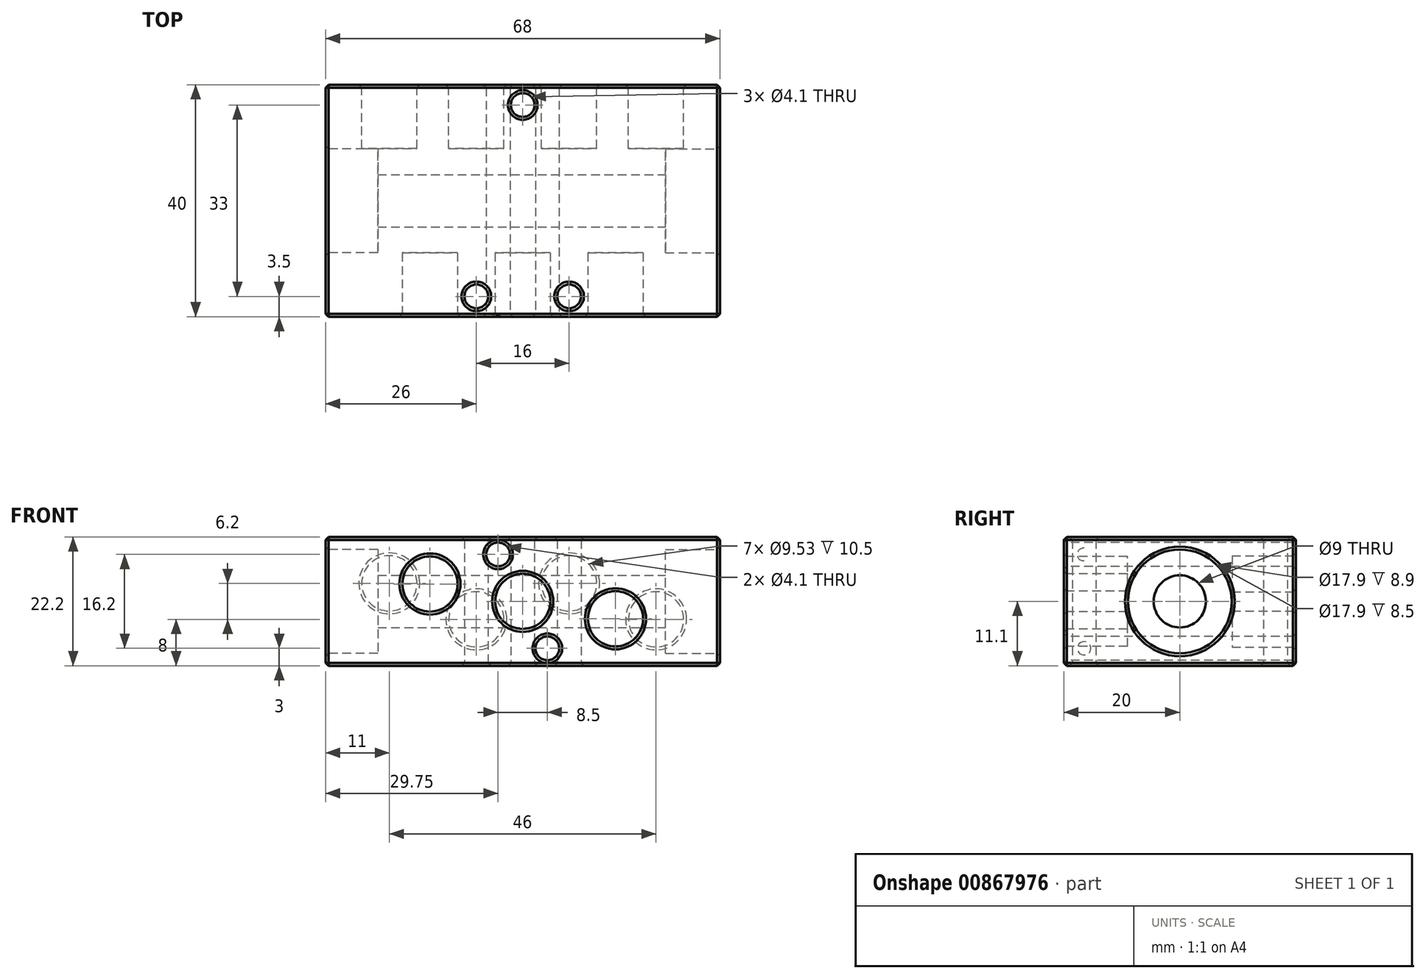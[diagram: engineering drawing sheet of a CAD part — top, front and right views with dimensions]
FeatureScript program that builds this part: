
annotation { "Feature Type Name" : "Feature", "Feature Type Description" : "" }
export const myFeature = defineFeature(function(context is Context, id is Id, definition is map)
    precondition{}
    {
        {
            var Q0;
            Q0=qCreatedBy(makeId("Top.planeOp"),FACE);
            var sketch = newSketch(context, id + "F0", { "sketchPlane" : qUnion([Q0])});
            skLineSegment(sketch, "E0.bottom", {"start": v(0, 0) * mm, "end": v(68, 0) * mm});
            skLineSegment(sketch, "E0.top", {"start": v(0, 40) * mm, "end": v(68, 40) * mm});
            skLineSegment(sketch, "E0.left", {"start": v(0, 0) * mm, "end": v(0, 40) * mm});
            skLineSegment(sketch, "E0.right", {"start": v(68, 0) * mm, "end": v(68, 40) * mm});
            skCircle(sketch, "E1", {"center": v(34, 36.5) * mm, "radius": 2.05 * mm});
            skLineSegment(sketch, "E2", {"start": v(34, 40) * mm, "end": v(34, 0) * mm, "construction": true});
            skCircle(sketch, "E3", {"center": v(26, 3.5) * mm, "radius": 2.05 * mm});
            skCircle(sketch, "E4.MirrorC", {"center": v(42, 3.5) * mm, "radius": 2.05 * mm});
            skSolve(sketch);
        }
        {
            var Q0;
            Q0 = qSketchRegion(id + "F0", true);
            extrude(context, id + "F1", {"entities" : qUnion([Q0]), "depth" : 22.2 * mm, "offsetDistance" : 25 * mm});
        }
        {
            var Q0;
            Q0=makeQuery(id+"F1.opExtrude","SWEPT_FACE",FACE,{"disambiguationData":[OSD([sQuery(id+"F0.wireOp",EDGE,"E0.bottom")])]});
            var sketch = newSketch(context, id + "F2", { "sketchPlane" : qUnion([Q0])});
            skLineSegment(sketch, "E5", {"start": v(0, 11.1) * mm, "end": v(68, 11.1) * mm, "construction": true});
            skLineSegment(sketch, "E6", {"start": v(34, 22.2) * mm, "end": v(34, 0) * mm, "construction": true});
            skCircle(sketch, "E7", {"center": v(34, 11.1) * mm, "radius": 4.76 * mm});
            skCircle(sketch, "E8", {"center": v(50, 8.1) * mm, "radius": 4.76 * mm});
            skCircle(sketch, "E9", {"center": v(18, 14.1) * mm, "radius": 4.76 * mm});
            skCircle(sketch, "E10", {"center": v(38.25, 3) * mm, "radius": 2.05 * mm});
            skCircle(sketch, "E11", {"center": v(29.75, 19.2) * mm, "radius": 2.05 * mm});
            skSolve(sketch);
        }
        {
            var Q0;
            Q0=makeQuery(id+"F2.imprint","IMPRINT",FACE,{"disambiguationData":[TD([[makeQuery(id+"F2.imprint","IMPRINT",EDGE,{"derivedFrom":sQuery(id+"F2.wireOp",EDGE,"E9")}),1.0]])]});
            var Q1;
            Q1=makeQuery(id+"F2.imprint","IMPRINT",FACE,{"disambiguationData":[TD([[makeQuery(id+"F2.imprint","IMPRINT",EDGE,{"derivedFrom":sQuery(id+"F2.wireOp",EDGE,"E7")}),1.0]])]});
            var Q2;
            Q2=makeQuery(id+"F2.imprint","IMPRINT",FACE,{"disambiguationData":[TD([[makeQuery(id+"F2.imprint","IMPRINT",EDGE,{"derivedFrom":sQuery(id+"F2.wireOp",EDGE,"E8")}),1.0]])]});
            extrude(context, id + "F3", {"entities" : qUnion([Q0, Q1, Q2]), "operationType" : NewBodyOperationType.REMOVE, "oppositeDirection" : true, "depth" : 11 * mm, "offsetDistance" : 25 * mm});
        }
        {
            var Q0;
            Q0=makeQuery(id+"F2.imprint","IMPRINT",FACE,{"disambiguationData":[TD([[makeQuery(id+"F2.imprint","IMPRINT",EDGE,{"derivedFrom":sQuery(id+"F2.wireOp",EDGE,"E11")}),1.0]])]});
            var Q1;
            Q1=makeQuery(id+"F2.imprint","IMPRINT",FACE,{"disambiguationData":[TD([[makeQuery(id+"F2.imprint","IMPRINT",EDGE,{"derivedFrom":sQuery(id+"F2.wireOp",EDGE,"E10")}),1.0]])]});
            extrude(context, id + "F4", {"entities" : qUnion([Q0, Q1]), "operationType" : NewBodyOperationType.REMOVE, "endBound" : BoundingType.THROUGH_ALL, "oppositeDirection" : true, "depth" : 25 * mm, "offsetDistance" : 25 * mm});
        }
        {
            var Q0;
            Q0=makeQuery(id+"F1.opExtrude","SWEPT_FACE",FACE,{"disambiguationData":[OSD([sQuery(id+"F0.wireOp",EDGE,"E0.top")])]});
            var sketch = newSketch(context, id + "F5", { "sketchPlane" : qUnion([Q0])});
            skLineSegment(sketch, "E12", {"start": v(-68, 11.1) * mm, "end": v(0, 11.1) * mm, "construction": true});
            skLineSegment(sketch, "E13", {"start": v(-34, 22.2) * mm, "end": v(-34, 0) * mm, "construction": true});
            skCircle(sketch, "E14", {"center": v(-42, 14.2) * mm, "radius": 4.76 * mm});
            skCircle(sketch, "E15", {"center": v(-26, 8) * mm, "radius": 4.76 * mm});
            skCircle(sketch, "E16", {"center": v(-11, 14.2) * mm, "radius": 4.76 * mm});
            skCircle(sketch, "E17", {"center": v(-57, 8) * mm, "radius": 4.76 * mm});
            skSolve(sketch);
        }
        {
            var Q0;
            Q0 = qSketchRegion(id + "F5", true);
            extrude(context, id + "F6", {"entities" : qUnion([Q0]), "operationType" : NewBodyOperationType.REMOVE, "oppositeDirection" : true, "depth" : 11 * mm, "offsetDistance" : 25 * mm});
        }
        {
            var Q0;
            Q0=makeQuery(id+"F1.opExtrude","SWEPT_FACE",FACE,{"disambiguationData":[OSD([sQuery(id+"F0.wireOp",EDGE,"E0.right")])]});
            var sketch = newSketch(context, id + "F7", { "sketchPlane" : qUnion([Q0])});
            skCircle(sketch, "E18", {"center": v(20, 11.1) * mm, "radius": 8.95 * mm});
            skSolve(sketch);
        }
        {
            var Q0;
            Q0 = qSketchRegion(id + "F7", true);
            extrude(context, id + "F8", {"entities" : qUnion([Q0]), "operationType" : NewBodyOperationType.REMOVE, "oppositeDirection" : true, "depth" : 9.4 * mm, "offsetDistance" : 25 * mm});
        }
        {
            var Q0;
            Q0=makeQuery(id+"F8.boolean.opBoolean","COPY",FACE,{"derivedFrom":makeQuery(id+"F8.opExtrude","CAP_FACE",FACE,{"disambiguationData":[OSD([sQuery(id+"F7.wireOp",EDGE,"E18")])],"isStart":false})});
            var sketch = newSketch(context, id + "F9", { "sketchPlane" : qUnion([Q0])});
            skCircle(sketch, "E19", {"center": v(20, 11.1) * mm, "radius": 4.5 * mm});
            skSolve(sketch);
        }
        {
            var Q0;
            Q0 = qSketchRegion(id + "F9", true);
            extrude(context, id + "F10", {"entities" : qUnion([Q0]), "operationType" : NewBodyOperationType.REMOVE, "endBound" : BoundingType.THROUGH_ALL, "oppositeDirection" : true, "depth" : 25 * mm, "offsetDistance" : 25 * mm});
        }
        {
            var Q0;
            Q0=makeQuery(id+"F1.opExtrude","SWEPT_FACE",FACE,{"disambiguationData":[OSD([sQuery(id+"F0.wireOp",EDGE,"E0.left")])]});
            var sketch = newSketch(context, id + "F11", { "sketchPlane" : qUnion([Q0])});
            skCircle(sketch, "E20", {"center": v(-20, 11.1) * mm, "radius": 8.95 * mm});
            skSolve(sketch);
        }
        {
            var Q0;
            Q0 = qSketchRegion(id + "F11", true);
            extrude(context, id + "F12", {"entities" : qUnion([Q0]), "operationType" : NewBodyOperationType.REMOVE, "oppositeDirection" : true, "depth" : 9 * mm, "offsetDistance" : 25 * mm});
        }
        {
            var Q0;
            Q0=makeQuery(id+"F1.opExtrude","CAP_FACE",FACE,{"disambiguationData":[OSD([sQuery(id+"F0.wireOp",EDGE,"E0.bottom"),sQuery(id+"F0.wireOp",EDGE,"E0.top"),sQuery(id+"F0.wireOp",EDGE,"E0.left"),sQuery(id+"F0.wireOp",EDGE,"E0.right"),sQuery(id+"F0.wireOp",EDGE,"E1"),sQuery(id+"F0.wireOp",EDGE,"E3"),sQuery(id+"F0.wireOp",EDGE,"E4.MirrorC")])],"isStart":false});
            var Q1;
            Q1=makeQuery(id+"F1.opExtrude","SWEPT_FACE",FACE,{"disambiguationData":[OSD([sQuery(id+"F0.wireOp",EDGE,"E0.bottom")])]});
            var Q2;
            Q2=makeQuery(id+"F1.opExtrude","SWEPT_FACE",FACE,{"disambiguationData":[OSD([sQuery(id+"F0.wireOp",EDGE,"E0.left")])]});
            var Q3;
            Q3=makeQuery(id+"F1.opExtrude","CAP_FACE",FACE,{"disambiguationData":[OSD([sQuery(id+"F0.wireOp",EDGE,"E0.bottom"),sQuery(id+"F0.wireOp",EDGE,"E0.top"),sQuery(id+"F0.wireOp",EDGE,"E0.left"),sQuery(id+"F0.wireOp",EDGE,"E0.right"),sQuery(id+"F0.wireOp",EDGE,"E1"),sQuery(id+"F0.wireOp",EDGE,"E3"),sQuery(id+"F0.wireOp",EDGE,"E4.MirrorC")])],"isStart":true});
            var Q4;
            Q4=makeQuery(id+"F1.opExtrude","SWEPT_FACE",FACE,{"disambiguationData":[OSD([sQuery(id+"F0.wireOp",EDGE,"E0.right")])]});
            var Q5;
            Q5=makeQuery(id+"F1.opExtrude","SWEPT_FACE",FACE,{"disambiguationData":[OSD([sQuery(id+"F0.wireOp",EDGE,"E0.top")])]});
            chamfer(context, id + "F13", {"entities" : qUnion([Q0, Q1, Q2, Q3, Q4, Q5]), "width" : 0.5 * mm, "tangentPropagation" : true});
        }
    });
